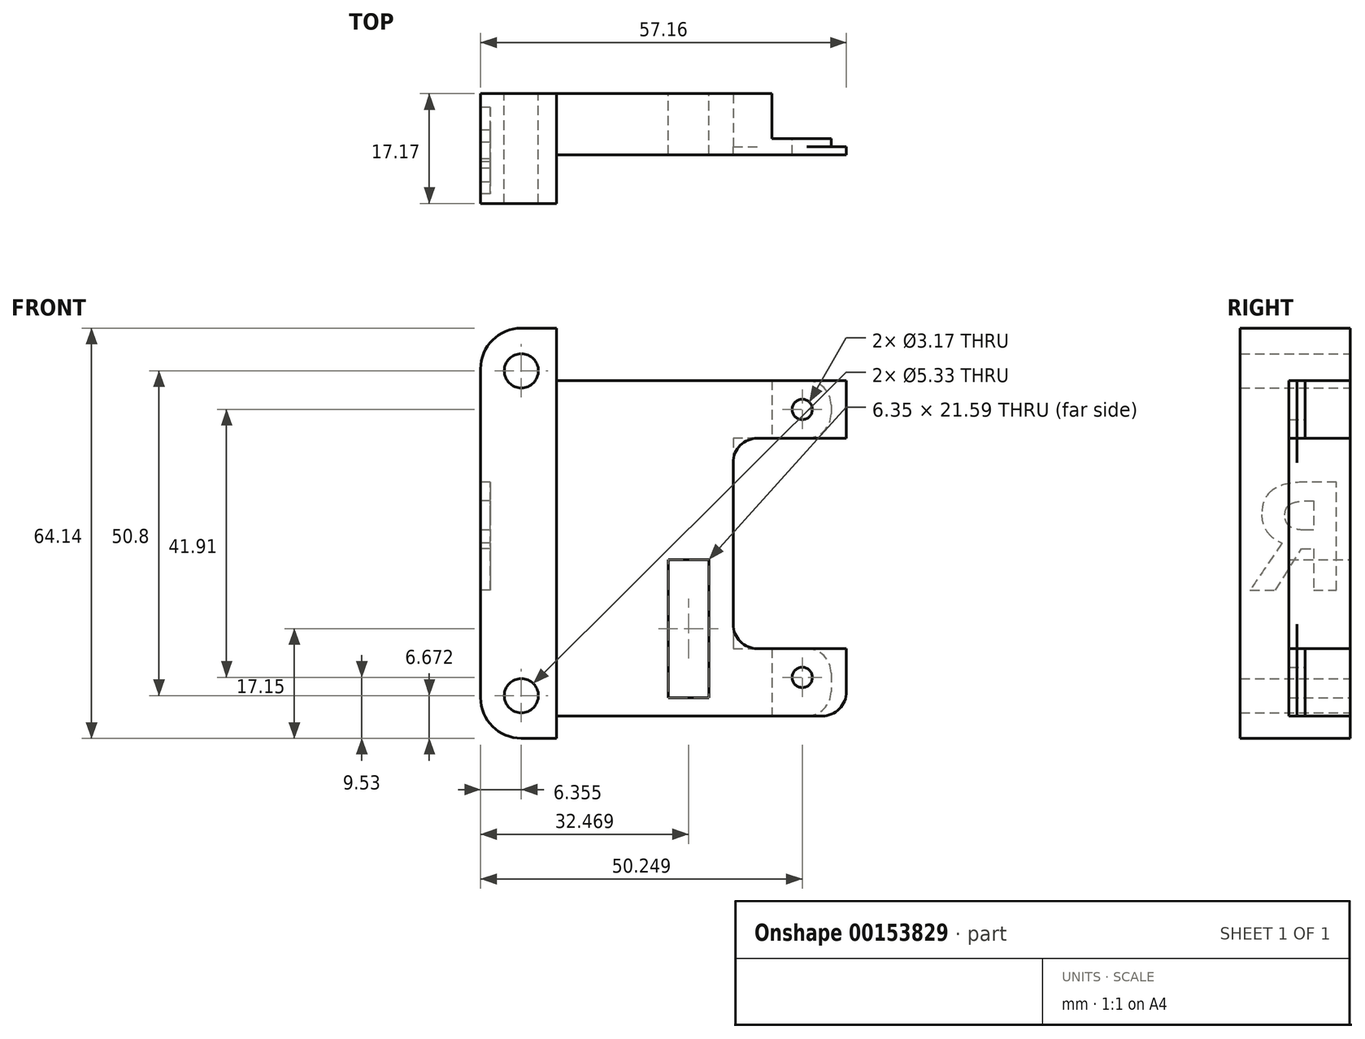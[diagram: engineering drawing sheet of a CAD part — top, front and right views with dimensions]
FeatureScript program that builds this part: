
annotation { "Feature Type Name" : "Feature", "Feature Type Description" : "" }
export const myFeature = defineFeature(function(context is Context, id is Id, definition is map)
    precondition{}
    {
        {
            var Q0;
            Q0=qCreatedBy(makeId("Front.planeOp"),FACE);
            var sketch = newSketch(context, id + "F0", { "sketchPlane" : qUnion([Q0])});
            skCircle(sketch, "E0", {"center": v(-136.53, -6.67) * mm, "radius": 2.67 * mm});
            skCircle(sketch, "E1", {"center": v(-136.53, -57.47) * mm, "radius": 2.67 * mm});
            skLineSegment(sketch, "E2.bottom", {"start": v(-136.53, 0) * mm, "end": v(-85.72, 0) * mm});
            skLineSegment(sketch, "E2.top", {"start": v(-136.53, -64.13) * mm, "end": v(-85.72, -64.13) * mm});
            skLineSegment(sketch, "E2.left", {"start": v(-142.88, -6.35) * mm, "end": v(-142.88, -57.78) * mm});
            skLineSegment(sketch, "E2.right", {"start": v(-85.72, 0) * mm, "end": v(-85.72, -64.13) * mm});
            skPoint(sketch, "E3.visualSharp", {"position": v(-142.88, 0) * mm});
            skArc(sketch, "E3.filletArc", {"start": v(-136.53, 0) * mm, "mid": v(-141.02, -1.86) * mm, "end": v(-142.87, -6.35) * mm});
            skPoint(sketch, "E4.visualSharp", {"position": v(-142.88, -64.13) * mm});
            skArc(sketch, "E4.filletArc", {"start": v(-142.87, -57.78) * mm, "mid": v(-141.02, -62.28) * mm, "end": v(-136.53, -64.13) * mm});
            skCircle(sketch, "E5", {"center": v(-92.63, -12.7) * mm, "radius": 1.59 * mm});
            skLineSegment(sketch, "E6", {"start": v(-136.53, -6.67) * mm, "end": v(-136.53, 0) * mm, "construction": true});
            skLineSegment(sketch, "E7", {"start": v(-136.53, -57.47) * mm, "end": v(-136.53, -64.13) * mm, "construction": true});
            skCircle(sketch, "E8", {"center": v(-92.63, -54.6) * mm, "radius": 1.59 * mm});
            skLineSegment(sketch, "E9.bottom", {"start": v(-113.59, -36.2) * mm, "end": v(-107.24, -36.2) * mm});
            skLineSegment(sketch, "E9.top", {"start": v(-113.59, -57.78) * mm, "end": v(-107.24, -57.78) * mm});
            skLineSegment(sketch, "E9.left", {"start": v(-107.24, -36.2) * mm, "end": v(-107.24, -57.78) * mm});
            skLineSegment(sketch, "E9.right", {"start": v(-113.59, -36.2) * mm, "end": v(-113.59, -57.78) * mm});
            skSolve(sketch);
        }
        {
            var Q0;
            Q0=makeQuery(id+"F0.imprint","IMPRINT",FACE,{"disambiguationData":[TD([[makeQuery(id+"F0.imprint","IMPRINT",EDGE,{"derivedFrom":sQuery(id+"F0.wireOp",EDGE,"E0")}),-1.0]])]});
            var Q1;
            Q1=makeQuery(id+"F0.imprint","IMPRINT",FACE,{"disambiguationData":[TD([[makeQuery(id+"F0.imprint","IMPRINT",EDGE,{"derivedFrom":sQuery(id+"F0.wireOp",EDGE,"01fd989c-5bba-4e2a-9568-51aa30f200c71.MirrorCS")}),1.0]])]});
            extrude(context, id + "F1", {"entities" : qUnion([Q0, Q1]), "depth" : 1.27 * mm});
        }
        {
            var Q0;
            Q0=makeQuery(id+"F1.opExtrude","CAP_FACE",FACE,{"disambiguationData":[OSD([sQuery(id+"F0.wireOp",EDGE,"E0"),sQuery(id+"F0.wireOp",EDGE,"E1"),sQuery(id+"F0.wireOp",EDGE,"E2.bottom"),sQuery(id+"F0.wireOp",EDGE,"E2.top"),sQuery(id+"F0.wireOp",EDGE,"E2.left"),sQuery(id+"F0.wireOp",EDGE,"E2.right"),sQuery(id+"F0.wireOp",EDGE,"E3.filletArc"),sQuery(id+"F0.wireOp",EDGE,"E4.filletArc"),sQuery(id+"F0.wireOp",EDGE,"E5"),sQuery(id+"F0.wireOp",EDGE,"E8"),sQuery(id+"F0.wireOp",EDGE,"E9.bottom"),sQuery(id+"F0.wireOp",EDGE,"E9.top"),sQuery(id+"F0.wireOp",EDGE,"E9.left"),sQuery(id+"F0.wireOp",EDGE,"E9.right")])],"isStart":true});
            var sketch = newSketch(context, id + "F2", { "sketchPlane" : qUnion([Q0])});
            skLineSegment(sketch, "E10", {"start": v(131.05, -64.13) * mm, "end": v(131.05, 0) * mm});
            skLineSegment(sketch, "E11", {"start": v(131.05, 0) * mm, "end": v(136.53, 0) * mm});
            skLineSegment(sketch, "E12", {"start": v(131.05, -64.13) * mm, "end": v(136.53, -64.13) * mm});
            skArc(sketch, "E13", {"start": v(136.53, -64.13) * mm, "mid": v(141.02, -62.28) * mm, "end": v(142.87, -57.78) * mm});
            skArc(sketch, "E14", {"start": v(136.53, 0) * mm, "mid": v(141.02, -1.86) * mm, "end": v(142.87, -6.35) * mm});
            skLineSegment(sketch, "E15", {"start": v(142.88, -57.78) * mm, "end": v(142.87, -6.35) * mm});
            skCircle(sketch, "E16", {"center": v(136.53, -57.47) * mm, "radius": 2.67 * mm});
            skCircle(sketch, "E17", {"center": v(136.53, -6.67) * mm, "radius": 2.67 * mm});
            skSolve(sketch);
        }
        {
            var Q0;
            Q0=makeQuery(id+"F2.imprint","IMPRINT",FACE,{"disambiguationData":[TD([[makeQuery(id+"F2.imprint","IMPRINT",EDGE,{"derivedFrom":sQuery(id+"F2.wireOp",EDGE,"E10")}),-1.0]])]});
            extrude(context, id + "F3", {"entities" : qUnion([Q0]), "operationType" : NewBodyOperationType.ADD, "depth" : 8.28 * mm, "hasSecondDirection" : true, "secondDirectionOppositeDirection" : true, "secondDirectionDepth" : 8.9 * mm});
        }
        {
            var Q0;
            Q0=makeQuery(id+"F1.opExtrude","CAP_FACE",FACE,{"disambiguationData":[OSD([sQuery(id+"F0.wireOp",EDGE,"E0"),sQuery(id+"F0.wireOp",EDGE,"E1"),sQuery(id+"F0.wireOp",EDGE,"E2.bottom"),sQuery(id+"F0.wireOp",EDGE,"E2.top"),sQuery(id+"F0.wireOp",EDGE,"E2.left"),sQuery(id+"F0.wireOp",EDGE,"E2.right"),sQuery(id+"F0.wireOp",EDGE,"E3.filletArc"),sQuery(id+"F0.wireOp",EDGE,"E4.filletArc"),sQuery(id+"F0.wireOp",EDGE,"E5"),sQuery(id+"F0.wireOp",EDGE,"E8"),sQuery(id+"F0.wireOp",EDGE,"E9.bottom"),sQuery(id+"F0.wireOp",EDGE,"E9.top"),sQuery(id+"F0.wireOp",EDGE,"E9.left"),sQuery(id+"F0.wireOp",EDGE,"E9.right")])],"isStart":true});
            var sketch = newSketch(context, id + "F4", { "sketchPlane" : qUnion([Q0])});
            skLineSegment(sketch, "E18.bottom", {"start": v(85.72, 0) * mm, "end": v(131.05, 0) * mm});
            skLineSegment(sketch, "E18.top", {"start": v(85.72, -8.2) * mm, "end": v(131.05, -8.2) * mm});
            skLineSegment(sketch, "E18.left", {"start": v(85.72, 0) * mm, "end": v(85.72, -8.2) * mm});
            skLineSegment(sketch, "E18.right", {"start": v(131.05, 0) * mm, "end": v(131.05, -8.2) * mm});
            skLineSegment(sketch, "E19.bottom", {"start": v(85.72, -64.13) * mm, "end": v(131.05, -64.13) * mm});
            skLineSegment(sketch, "E19.top", {"start": v(85.72, -60.64) * mm, "end": v(131.05, -60.64) * mm});
            skLineSegment(sketch, "E19.left", {"start": v(85.72, -64.13) * mm, "end": v(85.72, -60.64) * mm});
            skLineSegment(sketch, "E19.right", {"start": v(131.05, -64.13) * mm, "end": v(131.05, -60.64) * mm});
            skLineSegment(sketch, "E20.bottom", {"start": v(85.72, -17.2) * mm, "end": v(103.43, -17.2) * mm});
            skLineSegment(sketch, "E20.top", {"start": v(85.72, -50.1) * mm, "end": v(103.43, -50.1) * mm});
            skLineSegment(sketch, "E20.left", {"start": v(85.72, -17.2) * mm, "end": v(85.72, -50.1) * mm});
            skLineSegment(sketch, "E20.right", {"start": v(103.43, -17.2) * mm, "end": v(103.43, -50.1) * mm});
            skLineSegment(sketch, "E21.bottom", {"start": v(85.72, -8.2) * mm, "end": v(88.12, -8.2) * mm});
            skLineSegment(sketch, "E21.top", {"start": v(85.72, -17.2) * mm, "end": v(88.12, -17.2) * mm});
            skLineSegment(sketch, "E21.left", {"start": v(85.72, -8.2) * mm, "end": v(85.72, -17.2) * mm});
            skLineSegment(sketch, "E21.right", {"start": v(88.12, -8.2) * mm, "end": v(88.12, -17.2) * mm});
            skLineSegment(sketch, "E22.bottom", {"start": v(85.72, -50.1) * mm, "end": v(88.12, -50.1) * mm});
            skLineSegment(sketch, "E22.top", {"start": v(85.72, -60.64) * mm, "end": v(88.12, -60.64) * mm});
            skLineSegment(sketch, "E22.left", {"start": v(85.72, -50.1) * mm, "end": v(85.72, -60.64) * mm});
            skLineSegment(sketch, "E22.right", {"start": v(88.12, -50.1) * mm, "end": v(88.12, -60.64) * mm});
            skSolve(sketch);
        }
        {
            var Q0;
            Q0=makeQuery(id+"F4.imprint","IMPRINT",FACE,{"disambiguationData":[TD([[makeQuery(id+"F4.imprint","IMPRINT",EDGE,{"derivedFrom":sQuery(id+"F4.wireOp",EDGE,"E20.bottom")}),-1.0]])]});
            var Q1;
            Q1=makeQuery(id+"F4.imprint","IMPRINT",FACE,{"disambiguationData":[TD([[makeQuery(id+"F4.imprint","IMPRINT",EDGE,{"derivedFrom":sQuery(id+"F4.wireOp",EDGE,"E18.bottom")}),1.0]])]});
            var Q2;
            Q2=makeQuery(id+"F4.imprint","IMPRINT",FACE,{"disambiguationData":[TD([[makeQuery(id+"F4.imprint","IMPRINT",EDGE,{"derivedFrom":sQuery(id+"F4.wireOp",EDGE,"E19.bottom")}),-1.0]])]});
            var Q3;
            Q3=makeQuery(id+"F4.imprint","IMPRINT",FACE,{"disambiguationData":[TD([[makeQuery(id+"F4.imprint","IMPRINT",EDGE,{"derivedFrom":sQuery(id+"F4.wireOp",EDGE,"E22.bottom")}),-1.0]])]});
            var Q4;
            Q4=makeQuery(id+"F4.imprint","IMPRINT",FACE,{"disambiguationData":[TD([[makeQuery(id+"F4.imprint","IMPRINT",EDGE,{"derivedFrom":sQuery(id+"F4.wireOp",EDGE,"E21.bottom")}),-1.0]])]});
            extrude(context, id + "F5", {"entities" : qUnion([Q0, Q1, Q2, Q3, Q4]), "operationType" : NewBodyOperationType.REMOVE, "oppositeDirection" : true, "depth" : 25.4 * mm});
        }
        {
            var Q0;
            Q0=makeQuery(id+"F5.boolean.opBoolean","COPY",EDGE,{"derivedFrom":makeQuery(id+"F5.opExtrude","SWEPT_EDGE",EDGE,{"disambiguationData":[OSD([sQuery(id+"F4.wireOp",EDGE,"E18.top"),sQuery(id+"F4.wireOp",EDGE,"E21.bottom"),sQuery(id+"F4.wireOp",EDGE,"E21.right")])]})});
            var Q1;
            Q1=makeQuery(id+"F5.boolean.opBoolean","COPY",EDGE,{"derivedFrom":makeQuery(id+"F5.opExtrude","SWEPT_EDGE",EDGE,{"disambiguationData":[OSD([sQuery(id+"F4.wireOp",EDGE,"E20.bottom"),sQuery(id+"F4.wireOp",EDGE,"E21.top"),sQuery(id+"F4.wireOp",EDGE,"E21.right")])]})});
            var Q2;
            Q2=makeQuery(id+"F5.boolean.opBoolean","COPY",EDGE,{"derivedFrom":makeQuery(id+"F5.opExtrude","SWEPT_EDGE",EDGE,{"disambiguationData":[OSD([sQuery(id+"F4.wireOp",EDGE,"E20.top"),sQuery(id+"F4.wireOp",EDGE,"E22.bottom"),sQuery(id+"F4.wireOp",EDGE,"E22.right")])]})});
            var Q3;
            Q3=makeQuery(id+"F5.boolean.opBoolean","COPY",EDGE,{"derivedFrom":makeQuery(id+"F5.opExtrude","SWEPT_EDGE",EDGE,{"disambiguationData":[OSD([sQuery(id+"F4.wireOp",EDGE,"E19.top"),sQuery(id+"F4.wireOp",EDGE,"E22.top"),sQuery(id+"F4.wireOp",EDGE,"E22.right")])]})});
            fillet(context, id + "F6", {"entities" : qUnion([Q0, Q1, Q2, Q3]), "radius" : 3.8 * mm, "tangentPropagation" : true, "allowEdgeOverflow" : false});
        }
        {
            var Q0;
            Q0=makeQuery(id+"F1.opExtrude","CAP_FACE",FACE,{"disambiguationData":[OSD([sQuery(id+"F0.wireOp",EDGE,"E0"),sQuery(id+"F0.wireOp",EDGE,"E1"),sQuery(id+"F0.wireOp",EDGE,"E2.bottom"),sQuery(id+"F0.wireOp",EDGE,"E2.top"),sQuery(id+"F0.wireOp",EDGE,"E2.left"),sQuery(id+"F0.wireOp",EDGE,"E2.right"),sQuery(id+"F0.wireOp",EDGE,"E3.filletArc"),sQuery(id+"F0.wireOp",EDGE,"E4.filletArc"),sQuery(id+"F0.wireOp",EDGE,"E5"),sQuery(id+"F0.wireOp",EDGE,"E8"),sQuery(id+"F0.wireOp",EDGE,"E9.bottom"),sQuery(id+"F0.wireOp",EDGE,"E9.top"),sQuery(id+"F0.wireOp",EDGE,"E9.left"),sQuery(id+"F0.wireOp",EDGE,"E9.right")])],"isStart":true});
            var sketch = newSketch(context, id + "F7", { "sketchPlane" : qUnion([Q0])});
            skLineSegment(sketch, "E23.bottom", {"start": v(131.05, -8.2) * mm, "end": v(97.4, -8.2) * mm});
            skLineSegment(sketch, "E23.top", {"start": v(131.05, -60.64) * mm, "end": v(97.4, -60.64) * mm});
            skLineSegment(sketch, "E23.left", {"start": v(131.05, -8.2) * mm, "end": v(131.05, -60.64) * mm});
            skLineSegment(sketch, "E23.right", {"start": v(97.4, -8.2) * mm, "end": v(97.4, -17.2) * mm});
            skLineSegment(sketch, "E24.bottom", {"start": v(107.24, -36.2) * mm, "end": v(113.59, -36.2) * mm});
            skLineSegment(sketch, "E24.top", {"start": v(107.24, -57.78) * mm, "end": v(113.59, -57.78) * mm});
            skLineSegment(sketch, "E24.left", {"start": v(107.24, -36.2) * mm, "end": v(107.24, -57.78) * mm});
            skLineSegment(sketch, "E24.right", {"start": v(113.59, -36.2) * mm, "end": v(113.59, -57.78) * mm});
            skLineSegment(sketch, "E25.bottom", {"start": v(103.43, -17.2) * mm, "end": v(97.4, -17.2) * mm});
            skLineSegment(sketch, "E25.top", {"start": v(103.43, -50.1) * mm, "end": v(97.4, -50.1) * mm});
            skLineSegment(sketch, "E25.left", {"start": v(103.43, -17.2) * mm, "end": v(103.43, -50.1) * mm});
            skLineSegment(sketch, "E26.trimOffspring", {"start": v(97.4, -50.1) * mm, "end": v(97.4, -60.64) * mm});
            skSolve(sketch);
        }
        {
            var Q0;
            Q0 = qSketchRegion(id + "F7", true);
            var Q1;
            Q1=makeQuery(id+"F3.opExtrude","CAP_FACE",FACE,{"disambiguationData":[OSD([sQuery(id+"F2.wireOp",EDGE,"E10"),sQuery(id+"F2.wireOp",EDGE,"E11"),sQuery(id+"F2.wireOp",EDGE,"E12"),sQuery(id+"F2.wireOp",EDGE,"E13"),sQuery(id+"F2.wireOp",EDGE,"E14"),sQuery(id+"F2.wireOp",EDGE,"E15"),sQuery(id+"F2.wireOp",EDGE,"E16"),sQuery(id+"F2.wireOp",EDGE,"E17")])],"isStart":false});
            extrude(context, id + "F8", {"entities" : qUnion([Q0]), "operationType" : NewBodyOperationType.ADD, "endBound" : BoundingType.UP_TO_SURFACE, "endBoundEntityFace" : qUnion([Q1]), "depth" : 25.4 * mm});
        }
        {
            var Q0;
            {var subQ3=sQuery(id+"F0.wireOp",EDGE,"E5");Q0=makeQuery(id+"F8.boolean.opBoolean","SPLIT",FACE,{"disambiguationData":[TD([makeQuery(id+"F1.opExtrude","SWEPT_FACE",FACE,{"disambiguationData":[OSD([subQ3])]})])],"derivedFrom":makeQuery(id+"F1.opExtrude","CAP_FACE",FACE,{"disambiguationData":[OSD([sQuery(id+"F0.wireOp",EDGE,"E0"),sQuery(id+"F0.wireOp",EDGE,"E1"),sQuery(id+"F0.wireOp",EDGE,"E2.bottom"),sQuery(id+"F0.wireOp",EDGE,"E2.top"),sQuery(id+"F0.wireOp",EDGE,"E2.left"),sQuery(id+"F0.wireOp",EDGE,"E2.right"),sQuery(id+"F0.wireOp",EDGE,"E3.filletArc"),sQuery(id+"F0.wireOp",EDGE,"E4.filletArc"),subQ3,sQuery(id+"F0.wireOp",EDGE,"E8"),sQuery(id+"F0.wireOp",EDGE,"E9.bottom"),sQuery(id+"F0.wireOp",EDGE,"E9.top"),sQuery(id+"F0.wireOp",EDGE,"E9.left"),sQuery(id+"F0.wireOp",EDGE,"E9.right")])],"isStart":true})});}
            var sketch = newSketch(context, id + "F9", { "sketchPlane" : qUnion([Q0])});
            skCircle(sketch, "E27", {"center": v(92.63, -12.7) * mm, "radius": 1.59 * mm});
            skCircle(sketch, "E28", {"center": v(92.63, -54.6) * mm, "radius": 1.59 * mm});
            skLineSegment(sketch, "E29", {"start": v(91.93, -8.2) * mm, "end": v(97.4, -8.2) * mm});
            skLineSegment(sketch, "E30", {"start": v(97.4, -8.2) * mm, "end": v(97.4, -17.2) * mm});
            skLineSegment(sketch, "E31", {"start": v(97.4, -17.2) * mm, "end": v(91.93, -17.2) * mm});
            skLineSegment(sketch, "E32", {"start": v(91.93, -50.1) * mm, "end": v(97.4, -50.1) * mm});
            skLineSegment(sketch, "E33", {"start": v(97.4, -50.1) * mm, "end": v(97.4, -60.64) * mm});
            skLineSegment(sketch, "E34", {"start": v(97.4, -60.64) * mm, "end": v(91.93, -60.64) * mm});
            skLineSegment(sketch, "E35", {"start": v(88.12, -12) * mm, "end": v(88.12, -13.4) * mm});
            skLineSegment(sketch, "E36", {"start": v(88.12, -53.91) * mm, "end": v(88.12, -56.83) * mm});
            skArc(sketch, "E37", {"start": v(91.93, -8.2) * mm, "mid": v(89.24, -9.3) * mm, "end": v(88.12, -12) * mm});
            skArc(sketch, "E38", {"start": v(88.12, -13.4) * mm, "mid": v(89.24, -16.1) * mm, "end": v(91.93, -17.2) * mm});
            skArc(sketch, "E39", {"start": v(91.93, -50.1) * mm, "mid": v(89.24, -51.22) * mm, "end": v(88.12, -53.91) * mm});
            skArc(sketch, "E40", {"start": v(88.12, -56.83) * mm, "mid": v(89.24, -59.53) * mm, "end": v(91.93, -60.64) * mm});
            skSolve(sketch);
        }
        {
            var Q0;
            Q0 = qSketchRegion(id + "F9", true);
            extrude(context, id + "F10", {"entities" : qUnion([Q0]), "operationType" : NewBodyOperationType.ADD, "depth" : 1.27 * mm});
        }
        {
            var Q0;
            Q0=makeQuery(id+"F3.boolean.opBoolean","MERGE",FACE,{"derivedFrom":[makeQuery(id+"F1.opExtrude","SWEPT_FACE",FACE,{"disambiguationData":[OSD([sQuery(id+"F0.wireOp",EDGE,"E2.left")])]}),makeQuery(id+"F3.opExtrude","SWEPT_FACE",FACE,{"disambiguationData":[OSD([sQuery(id+"F2.wireOp",EDGE,"E15")])]})]});
            var sketch = newSketch(context, id + "F11", { "sketchPlane" : qUnion([Q0])});
            skText(sketch, "E41", { "text": "R", "fontName": "OpenSans-Bold.ttf"});
            const initialGuessF11  = {"E41": [-0.00828, -0.04099, 1, 0, 0.01705]};
            skSetInitialGuess(sketch, initialGuessF11);
            skSolve(sketch);
        }
        {
            var Q0;
            Q0 = qSketchRegion(id + "F11", true);
            extrude(context, id + "F12", {"entities" : qUnion([Q0]), "operationType" : NewBodyOperationType.REMOVE, "oppositeDirection" : true, "depth" : 1.52 * mm});
        }
    });
